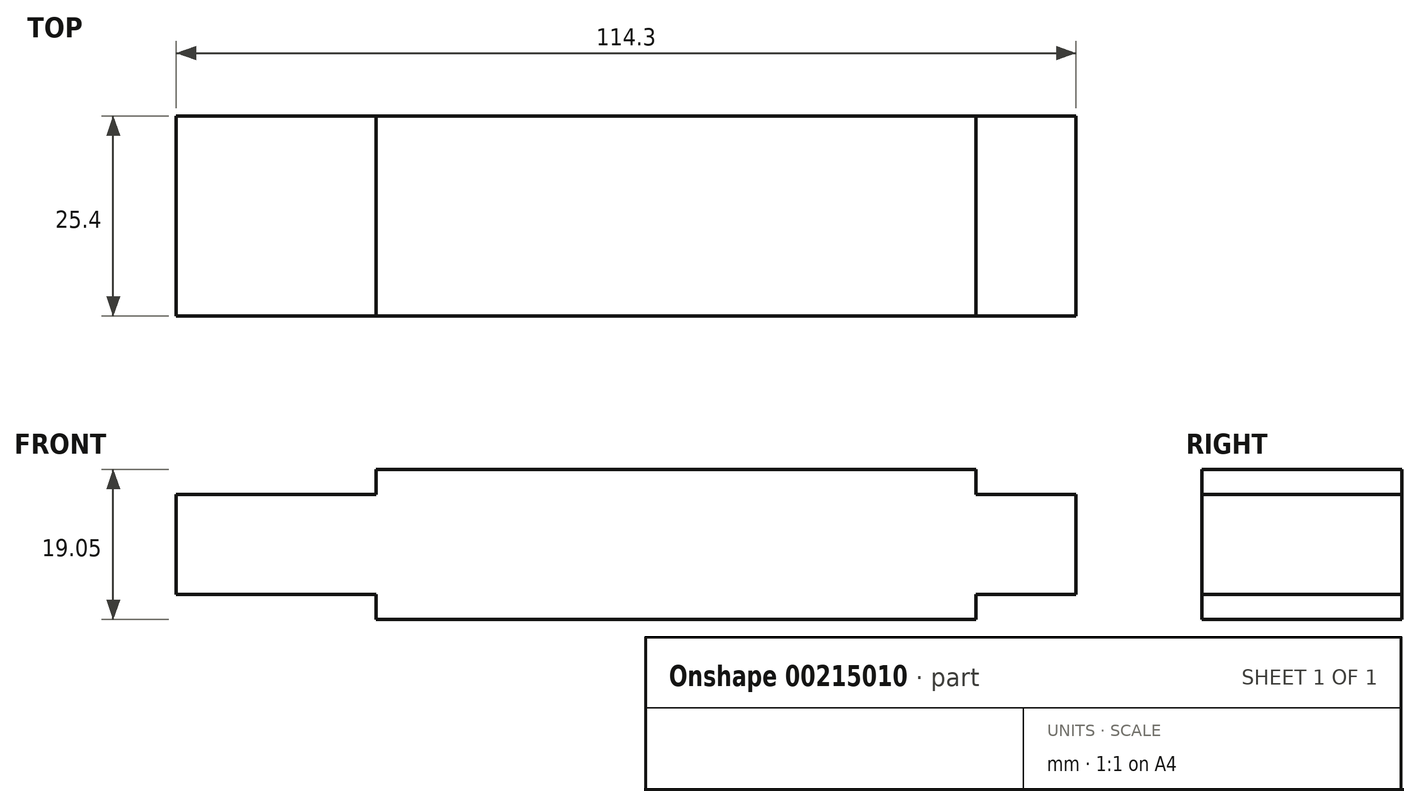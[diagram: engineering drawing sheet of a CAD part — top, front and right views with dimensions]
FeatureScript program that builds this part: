
annotation { "Feature Type Name" : "Feature", "Feature Type Description" : "" }
export const myFeature = defineFeature(function(context is Context, id is Id, definition is map)
    precondition{}
    {
        {
            var Q0;
            Q0=qCreatedBy(makeId("Front.planeOp"),FACE);
            var sketch = newSketch(context, id + "F0", { "sketchPlane" : qUnion([Q0])});
            skLineSegment(sketch, "E0.bottom", {"start": v(0, 0) * mm, "end": v(76.2, 0) * mm});
            skLineSegment(sketch, "E0.top", {"start": v(0, 19.05) * mm, "end": v(76.2, 19.05) * mm});
            skLineSegment(sketch, "E0.left", {"start": v(0, 0) * mm, "end": v(0, 19.05) * mm});
            skLineSegment(sketch, "E0.right", {"start": v(76.2, 0) * mm, "end": v(76.2, 19.05) * mm});
            skLineSegment(sketch, "E1.bottom", {"start": v(0, 15.88) * mm, "end": v(-25.4, 15.87) * mm});
            skLineSegment(sketch, "E1.top", {"start": v(0, 3.18) * mm, "end": v(-25.4, 3.17) * mm});
            skLineSegment(sketch, "E1.left", {"start": v(0, 15.88) * mm, "end": v(0, 3.18) * mm});
            skLineSegment(sketch, "E1.right", {"start": v(-25.4, 15.87) * mm, "end": v(-25.4, 3.17) * mm});
            skLineSegment(sketch, "E2.bottom", {"start": v(76.2, 3.18) * mm, "end": v(88.9, 3.18) * mm});
            skLineSegment(sketch, "E2.top", {"start": v(76.2, 15.88) * mm, "end": v(88.9, 15.88) * mm});
            skLineSegment(sketch, "E2.left", {"start": v(76.2, 3.18) * mm, "end": v(76.2, 15.88) * mm});
            skLineSegment(sketch, "E2.right", {"start": v(88.9, 3.18) * mm, "end": v(88.9, 15.88) * mm});
            skSolve(sketch);
        }
        {
            var Q0;
            Q0 = qSketchRegion(id + "F0", true);
            extrude(context, id + "F1", {"entities" : qUnion([Q0]), "endBound" : BoundingType.SYMMETRIC, "depth" : 25.4 * mm});
        }
    });
